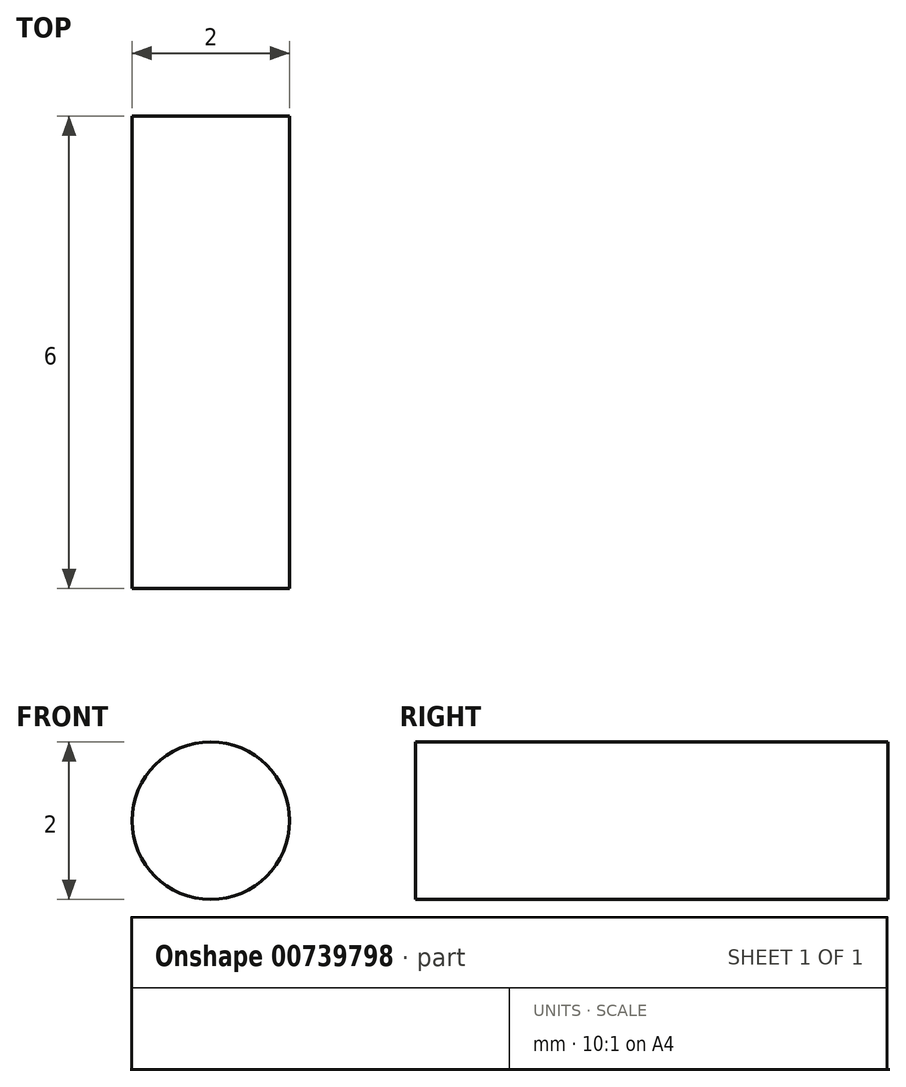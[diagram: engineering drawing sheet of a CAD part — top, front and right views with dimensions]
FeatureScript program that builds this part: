
annotation { "Feature Type Name" : "Feature", "Feature Type Description" : "" }
export const myFeature = defineFeature(function(context is Context, id is Id, definition is map)
    precondition{}
    {
        {
            var Q0;
            Q0=qCreatedBy(makeId("Front.planeOp"),FACE);
            var sketch = newSketch(context, id + "F0", { "sketchPlane" : qUnion([Q0])});
            skCircle(sketch, "E0", {"center": v(0, 0) * mm, "radius": 1 * mm});
            skSolve(sketch);
        }
        {
            var Q0;
            Q0 = qSketchRegion(id + "F0", true);
            extrude(context, id + "F1", {"entities" : qUnion([Q0]), "depth" : 6 * mm, "offsetDistance" : 25 * mm});
        }
    });
